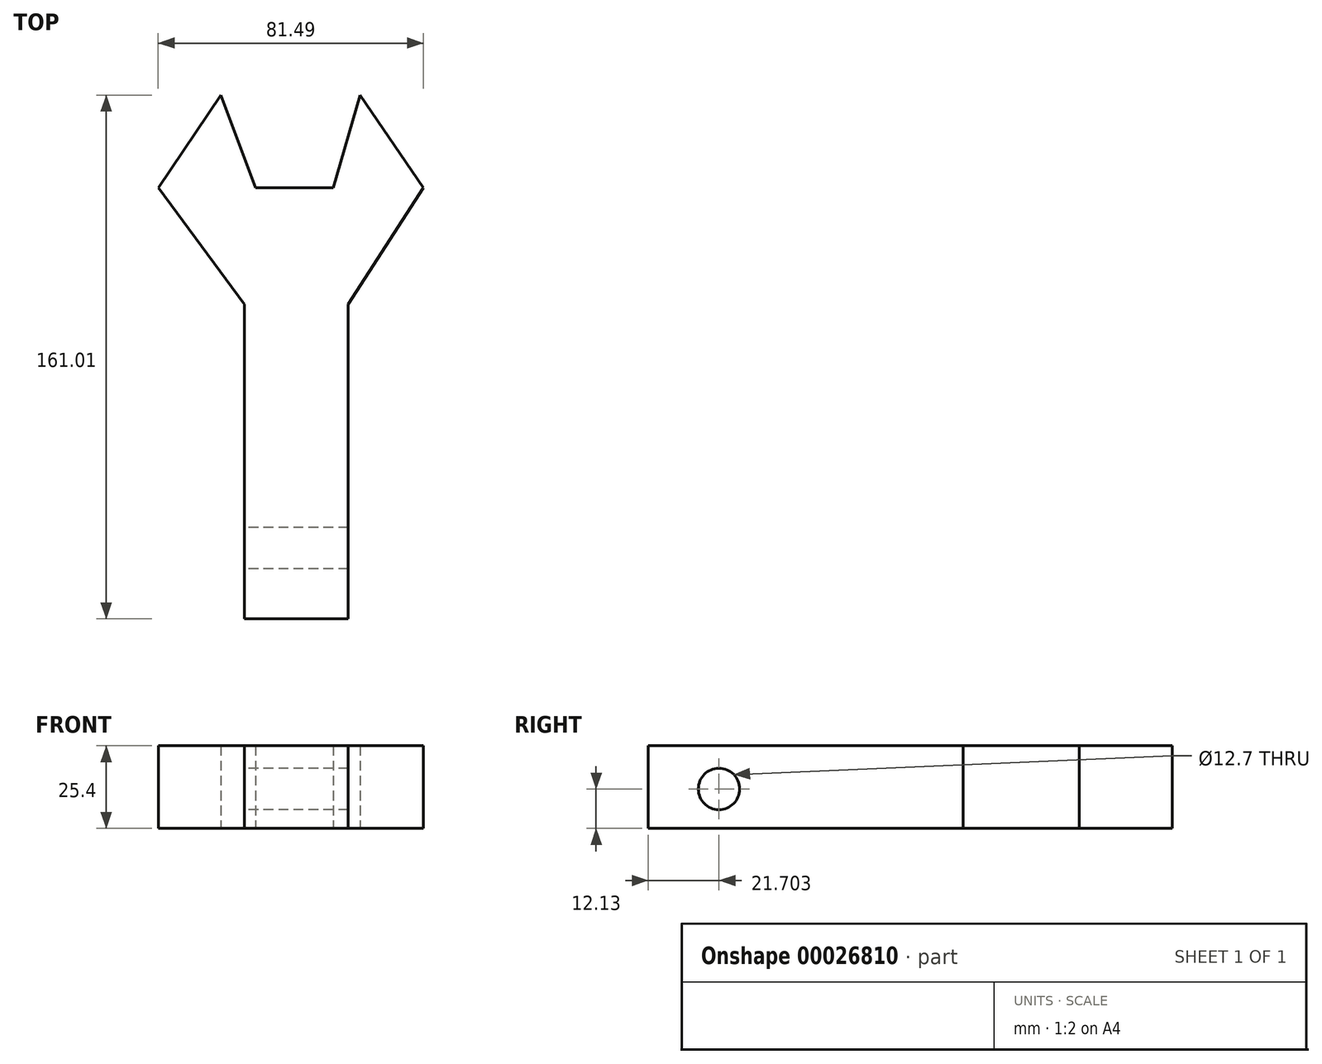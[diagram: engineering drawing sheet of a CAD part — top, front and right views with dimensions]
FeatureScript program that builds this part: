
annotation { "Feature Type Name" : "Feature", "Feature Type Description" : "" }
export const myFeature = defineFeature(function(context is Context, id is Id, definition is map)
    precondition{}
    {
        {
            var Q0;
            Q0=qCreatedBy(makeId("Top.planeOp"),FACE);
            var sketch = newSketch(context, id + "F0", { "sketchPlane" : qUnion([Q0])});
            skLineSegment(sketch, "E0.bottom", {"start": v(-20.1, -33.83) * mm, "end": v(11.74, -33.83) * mm});
            skLineSegment(sketch, "E0.top", {"start": v(-20.1, 20.3) * mm, "end": v(11.74, 20.3) * mm});
            skLineSegment(sketch, "E0.left", {"start": v(-20.1, -33.83) * mm, "end": v(-20.1, 20.3) * mm});
            skLineSegment(sketch, "E0.right", {"start": v(11.74, -33.83) * mm, "end": v(11.74, 20.3) * mm});
            skLineSegment(sketch, "E1", {"start": v(-20.1, 20.3) * mm, "end": v(-46.64, 56) * mm});
            skLineSegment(sketch, "E2", {"start": v(-46.64, 56) * mm, "end": v(-27.42, 84.57) * mm});
            skLineSegment(sketch, "E3", {"start": v(-27.42, 84.57) * mm, "end": v(-16.68, 56) * mm});
            skLineSegment(sketch, "E4", {"start": v(-16.68, 56) * mm, "end": v(7.09, 56) * mm});
            skLineSegment(sketch, "E5", {"start": v(7.09, 56) * mm, "end": v(15.4, 84.57) * mm});
            skLineSegment(sketch, "E6", {"start": v(15.4, 84.57) * mm, "end": v(34.85, 56) * mm});
            skLineSegment(sketch, "E7", {"start": v(34.85, 56) * mm, "end": v(11.74, 20.3) * mm});
            skLineSegment(sketch, "E8", {"start": v(-20.1, -33.83) * mm, "end": v(-20.1, -76.44) * mm});
            skLineSegment(sketch, "E9", {"start": v(-20.1, -76.44) * mm, "end": v(11.74, -76.44) * mm});
            skLineSegment(sketch, "E10", {"start": v(11.74, -76.44) * mm, "end": v(11.74, -33.83) * mm});
            skSolve(sketch);
        }
        {
            var Q0;
            Q0=makeQuery(id+"F0.imprint","IMPRINT",FACE,{"disambiguationData":[TD([[makeQuery(id+"F0.imprint","IMPRINT",EDGE,{"derivedFrom":sQuery(id+"F0.wireOp",EDGE,"E0.top")}),1.0]])]});
            var Q1;
            Q1=makeQuery(id+"F0.imprint","IMPRINT",FACE,{"disambiguationData":[TD([[makeQuery(id+"F0.imprint","IMPRINT",EDGE,{"derivedFrom":sQuery(id+"F0.wireOp",EDGE,"E0.bottom")}),1.0]])]});
            var Q2;
            Q2=makeQuery(id+"F0.imprint","IMPRINT",FACE,{"disambiguationData":[TD([[makeQuery(id+"F0.imprint","IMPRINT",EDGE,{"derivedFrom":sQuery(id+"F0.wireOp",EDGE,"E0.bottom")}),-1.0]])]});
            extrude(context, id + "F1", {"entities" : qUnion([Q0, Q1, Q2]), "depth" : 25.4 * mm});
        }
        {
            var Q0;
            Q0=makeQuery(id+"F1.opExtrude","SWEPT_FACE",FACE,{"disambiguationData":[OSD([sQuery(id+"F0.wireOp",EDGE,"E0.left")])]});
            var sketch = newSketch(context, id + "F2", { "sketchPlane" : qUnion([Q0])});
            skCircle(sketch, "E11", {"center": v(54.74, 12.13) * mm, "radius": 6.35 * mm});
            skSolve(sketch);
        }
        {
            var Q0;
            Q0=makeQuery(id+"F2.imprint","IMPRINT",FACE,{"disambiguationData":[TD([[makeQuery(id+"F2.imprint","IMPRINT",EDGE,{"derivedFrom":sQuery(id+"F2.wireOp",EDGE,"E11")}),1.0]])]});
            extrude(context, id + "F3", {"entities" : qUnion([Q0]), "operationType" : NewBodyOperationType.REMOVE, "oppositeDirection" : true, "depth" : 50.86 * mm});
        }
    });
